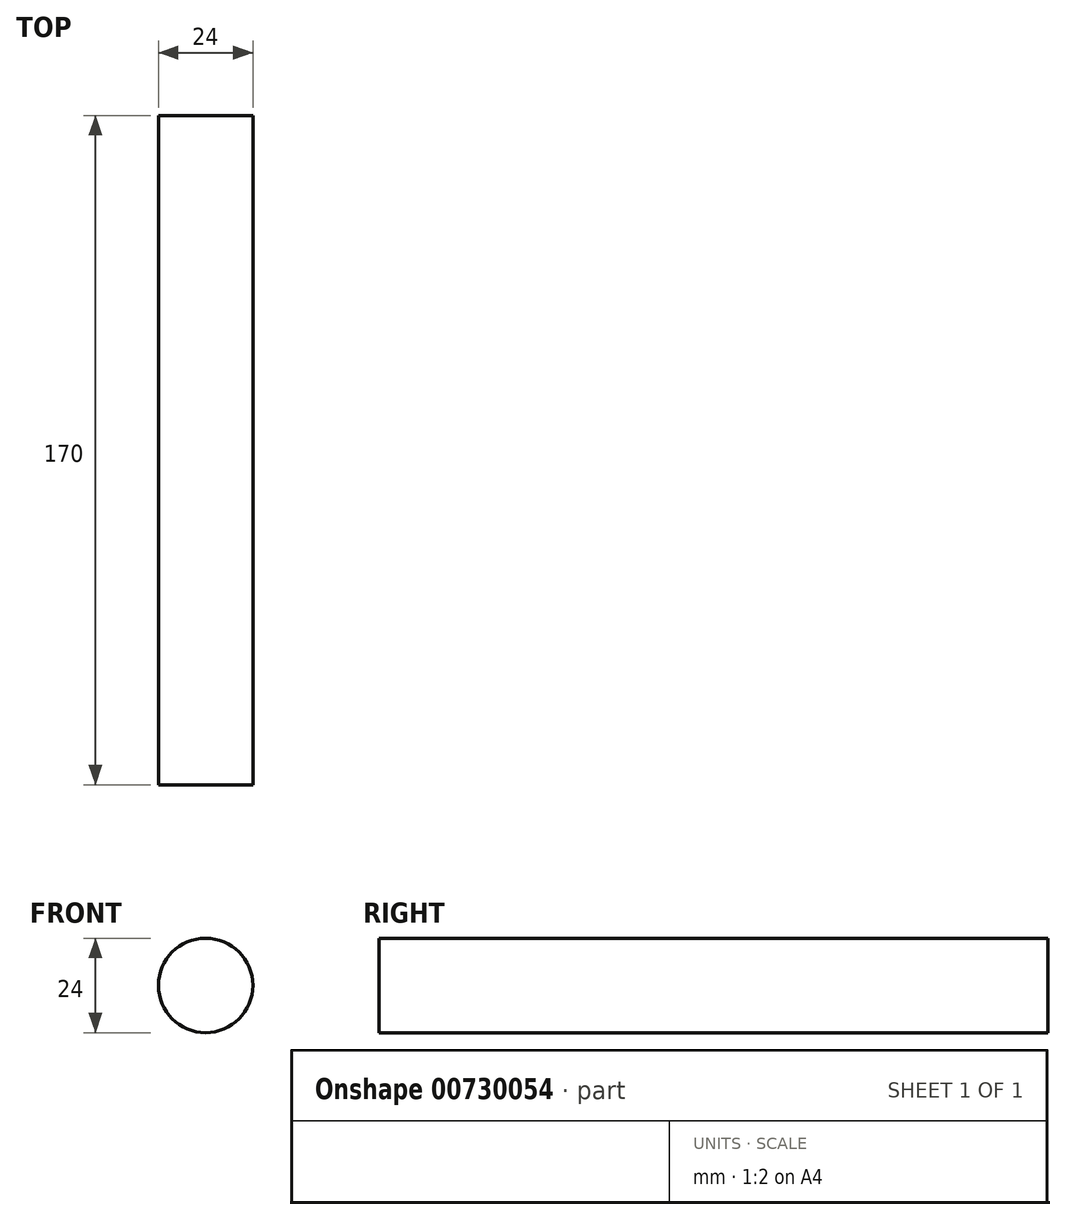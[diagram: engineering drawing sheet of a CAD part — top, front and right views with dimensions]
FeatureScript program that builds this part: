
annotation { "Feature Type Name" : "Feature", "Feature Type Description" : "" }
export const myFeature = defineFeature(function(context is Context, id is Id, definition is map)
    precondition{}
    {
        {
            var Q0;
            Q0=qCreatedBy(makeId("Front.planeOp"),FACE);
            var sketch = newSketch(context, id + "F0", { "sketchPlane" : qUnion([Q0])});
            skCircle(sketch, "E0", {"center": v(0, 0) * mm, "radius": 12 * mm});
            skSolve(sketch);
        }
        {
            var Q0;
            Q0=makeQuery(id+"F0.imprint","IMPRINT",FACE,{"disambiguationData":[TD([[makeQuery(id+"F0.imprint","IMPRINT",EDGE,{"derivedFrom":sQuery(id+"F0.wireOp",EDGE,"E0")}),1.0]])]});
            extrude(context, id + "F1", {"entities" : qUnion([Q0]), "depth" : 170 * mm, "offsetDistance" : 25 * mm});
        }
    });
